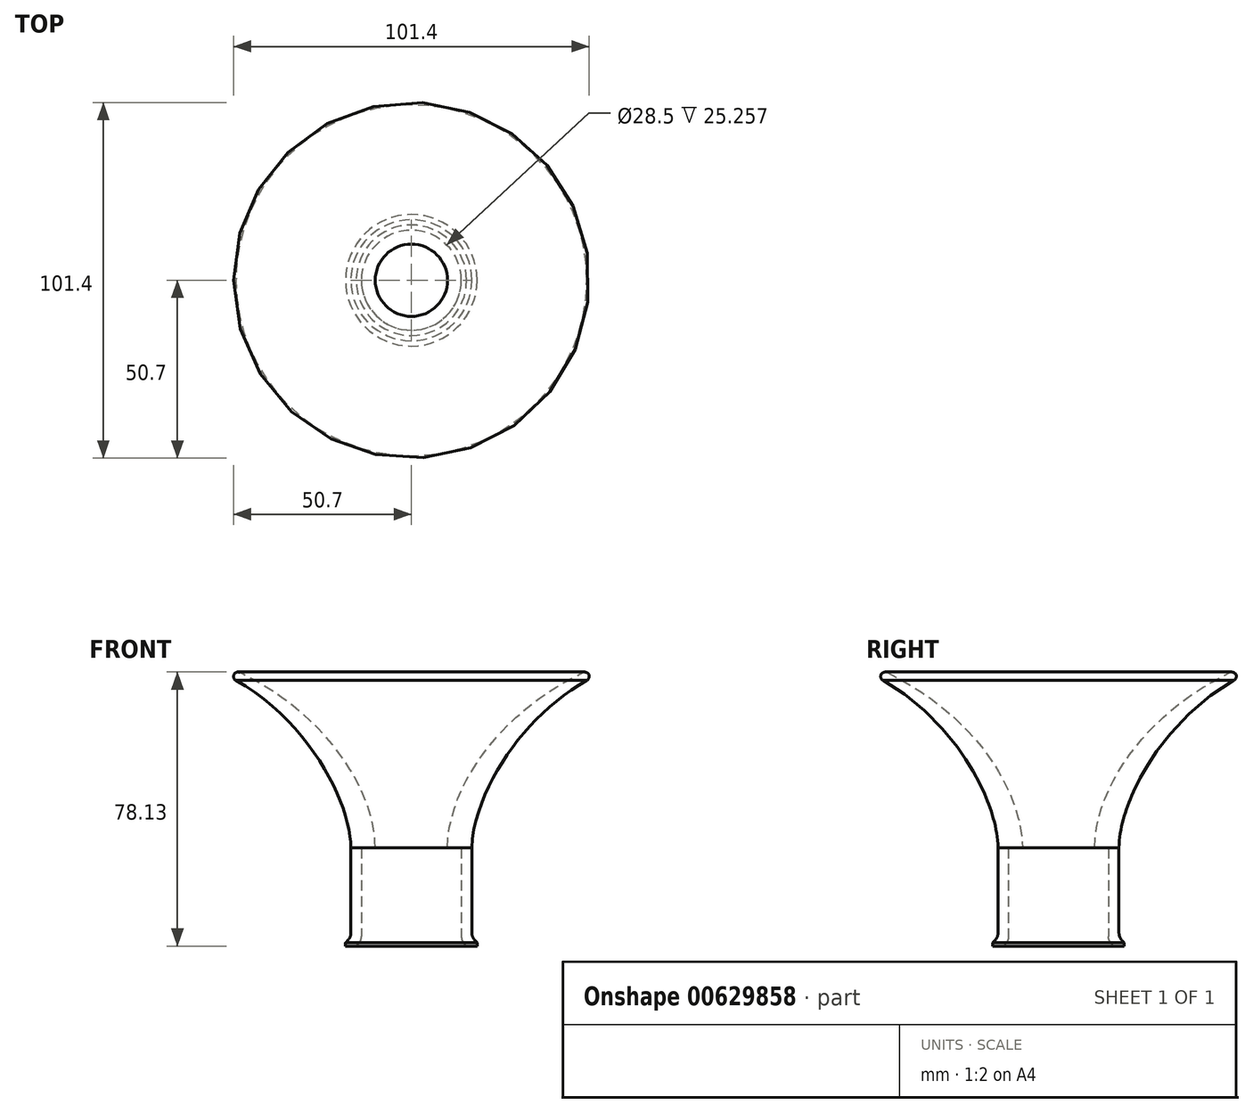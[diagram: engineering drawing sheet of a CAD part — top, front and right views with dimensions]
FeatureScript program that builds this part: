
annotation { "Feature Type Name" : "Feature", "Feature Type Description" : "" }
export const myFeature = defineFeature(function(context is Context, id is Id, definition is map)
    precondition{}
    {
        {
            var Q0;
            Q0=qCreatedBy(makeId("Front.planeOp"),FACE);
            var sketch = newSketch(context, id + "F0", { "sketchPlane" : qUnion([Q0])});
            skLineSegment(sketch, "E0", {"start": v(15.75, 0) * mm, "end": v(14.25, 1.5) * mm});
            skLineSegment(sketch, "E1", {"start": v(14.25, 1.5) * mm, "end": v(14.25, 28) * mm});
            skLineSegment(sketch, "E2", {"start": v(15.75, 0) * mm, "end": v(18.75, 0) * mm});
            skLineSegment(sketch, "E3", {"start": v(17.25, 2.5) * mm, "end": v(17.25, 28) * mm});
            skLineSegment(sketch, "E4", {"start": v(0, -0.9) * mm, "end": v(0, 24) * mm, "construction": true});
            skFitSpline(sketch, "E5", {"points": [v(17.25, 28) * mm, v(50, 75.75) * mm], "startDerivative": vector(0, 35.94) * mm, "endDerivative": vector(65.12, 37.22) * mm});
            skLineSegment(sketch, "E6", {"start": v(14.25, 28) * mm, "end": v(10.3, 28) * mm});
            skFitSpline(sketch, "E7", {"points": [v(10.3, 28) * mm, v(48.9, 78) * mm], "startDerivative": vector(0, 45.6) * mm, "endDerivative": vector(78.2, 38.07) * mm});
            skLineSegment(sketch, "E8", {"start": v(48.9, 78) * mm, "end": v(50, 75.75) * mm, "construction": true});
            skLineSegment(sketch, "E9", {"start": v(48.9, 78) * mm, "end": v(52.87, 79.93) * mm, "construction": true});
            skArc(sketch, "E10", {"start": v(50, 75.75) * mm, "mid": v(50.58, 77.42) * mm, "end": v(48.9, 78) * mm});
            skLineSegment(sketch, "E11", {"start": v(17.25, 2.5) * mm, "end": v(18.75, 1) * mm});
            skLineSegment(sketch, "E12", {"start": v(18.75, 1) * mm, "end": v(18.75, 0) * mm});
            skPoint(sketch, "E13.orphan", {"position": v(17.25, 0) * mm});
            skSolve(sketch);
        }
        {
            var Q0;
            Q0=makeQuery(id+"F0.imprint","IMPRINT",FACE,{"disambiguationData":[TD([[makeQuery(id+"F0.imprint","IMPRINT",EDGE,{"derivedFrom":sQuery(id+"F0.wireOp",EDGE,"E0")}),-1.0]])]});
            var Q1;
            Q1=sQuery(id+"F0.wireOp",EDGE,"E4");
            revolve(context, id + "F1", {"entities" : qUnion([Q0]), "axis" : qUnion([Q1]), "revolveType" : RevolveType.FULL});
        }
        {
            var Q0;
            Q0=makeQuery(id+"F1.opRevolve","SWEPT_EDGE",EDGE,{"disambiguationData":[OSD([sQuery(id+"F0.wireOp",EDGE,"E3"),sQuery(id+"F0.wireOp",EDGE,"E11")])]});
            var Q1;
            Q1=makeQuery(id+"F1.opRevolve","SWEPT_EDGE",EDGE,{"disambiguationData":[OSD([sQuery(id+"F0.wireOp",EDGE,"E0"),sQuery(id+"F0.wireOp",EDGE,"E1")])]});
            fillet(context, id + "F2", {"entities" : qUnion([Q0, Q1]), "radius" : 3 * mm, "tangentPropagation" : true, "allowEdgeOverflow" : false});
        }
    });
